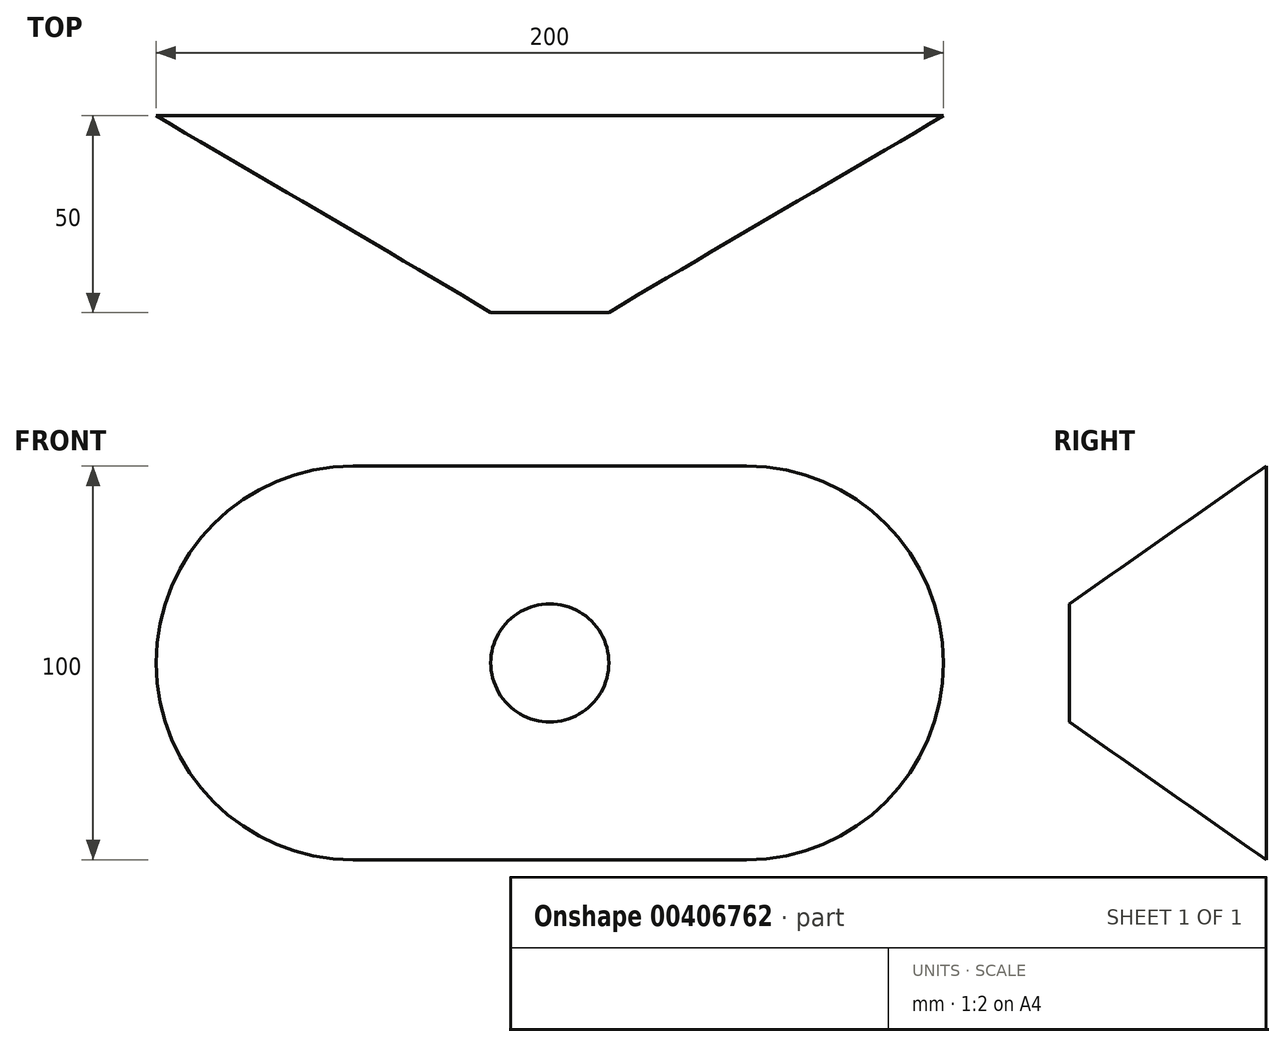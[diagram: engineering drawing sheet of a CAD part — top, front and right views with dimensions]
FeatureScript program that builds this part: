
annotation { "Feature Type Name" : "Feature", "Feature Type Description" : "" }
export const myFeature = defineFeature(function(context is Context, id is Id, definition is map)
    precondition{}
    {
        {
            var Q0;
            Q0=qCreatedBy(makeId("Front.planeOp"),FACE);
            var sketch = newSketch(context, id + "F0", { "sketchPlane" : qUnion([Q0])});
            skCircle(sketch, "E0", {"center": v(0, 0) * mm, "radius": 15 * mm});
            skSolve(sketch);
        }
        {
            var Q0;
            Q0=qCreatedBy(makeId("Front.planeOp"),FACE);
            cPlane(context, id + "F1", {"entities" : qUnion([Q0]), "cplaneType" : CPlaneType.OFFSET, "offset" : 50 * mm, "oppositeDirection" : true, "width" : 150 * mm, "height" : 150 * mm});
        }
        {
            var Q0;
            Q0=qCreatedBy(id+"F1.planeOp",FACE);
            var sketch = newSketch(context, id + "F2", { "sketchPlane" : qUnion([Q0])});
            skLineSegment(sketch, "E1.bottom", {"start": v(-50, 50) * mm, "end": v(50, 50) * mm});
            skLineSegment(sketch, "E1.top", {"start": v(-50, -50) * mm, "end": v(50, -50) * mm});
            skLineSegment(sketch, "E1.left", {"start": v(-100, 0) * mm, "end": v(-100, 0) * mm});
            skLineSegment(sketch, "E1.right", {"start": v(100, 0) * mm, "end": v(100, 0) * mm});
            skPoint(sketch, "E1.middle", {"position": v(0, 0) * mm});
            skPoint(sketch, "E2.visualSharp", {"position": v(100, 50) * mm});
            skArc(sketch, "E2.filletArc", {"start": v(100, 0) * mm, "mid": v(85.36, 35.36) * mm, "end": v(50, 50) * mm});
            skPoint(sketch, "E3.visualSharp", {"position": v(100, -50) * mm});
            skArc(sketch, "E3.filletArc", {"start": v(50, -50) * mm, "mid": v(85.36, -35.36) * mm, "end": v(100, 0) * mm});
            skPoint(sketch, "E4.visualSharp", {"position": v(-100, -50) * mm});
            skArc(sketch, "E4.filletArc", {"start": v(-100, 0) * mm, "mid": v(-85.36, -35.36) * mm, "end": v(-50, -50) * mm});
            skPoint(sketch, "E5.visualSharp", {"position": v(-100, 50) * mm});
            skArc(sketch, "E5.filletArc", {"start": v(-50, 50) * mm, "mid": v(-85.36, 35.36) * mm, "end": v(-100, 0) * mm});
            skSolve(sketch);
        }
        {
            var Q0;
            Q0=makeQuery(id+"F0.imprint","IMPRINT",FACE,{"disambiguationData":[TD([[makeQuery(id+"F0.imprint","IMPRINT",EDGE,{"derivedFrom":sQuery(id+"F0.wireOp",EDGE,"E0")}),1.0]])]});
            var Q1;
            Q1=makeQuery(id+"F2.imprint","IMPRINT",FACE,{"disambiguationData":[TD([[makeQuery(id+"F2.imprint","IMPRINT",EDGE,{"derivedFrom":sQuery(id+"F2.wireOp",EDGE,"E1.bottom")}),-1.0]])]});
            var Q2;
            Q2=sQuery(id+"F2.wireOp",VERTEX,"E2.filletArc.end");
            loft(context, id + "F3", {"sheetProfilesArray" : [{ "sheetProfileEntities" : qUnion([Q0]) }, { "sheetProfileEntities" : qUnion([Q1]) }], "connections" : [{ "connectionEntities" : qUnion([Q2]), "connectionEdgeQueries" : qUnion([]), "connectionEdgeParameters" : [] }]});
        }
    });
